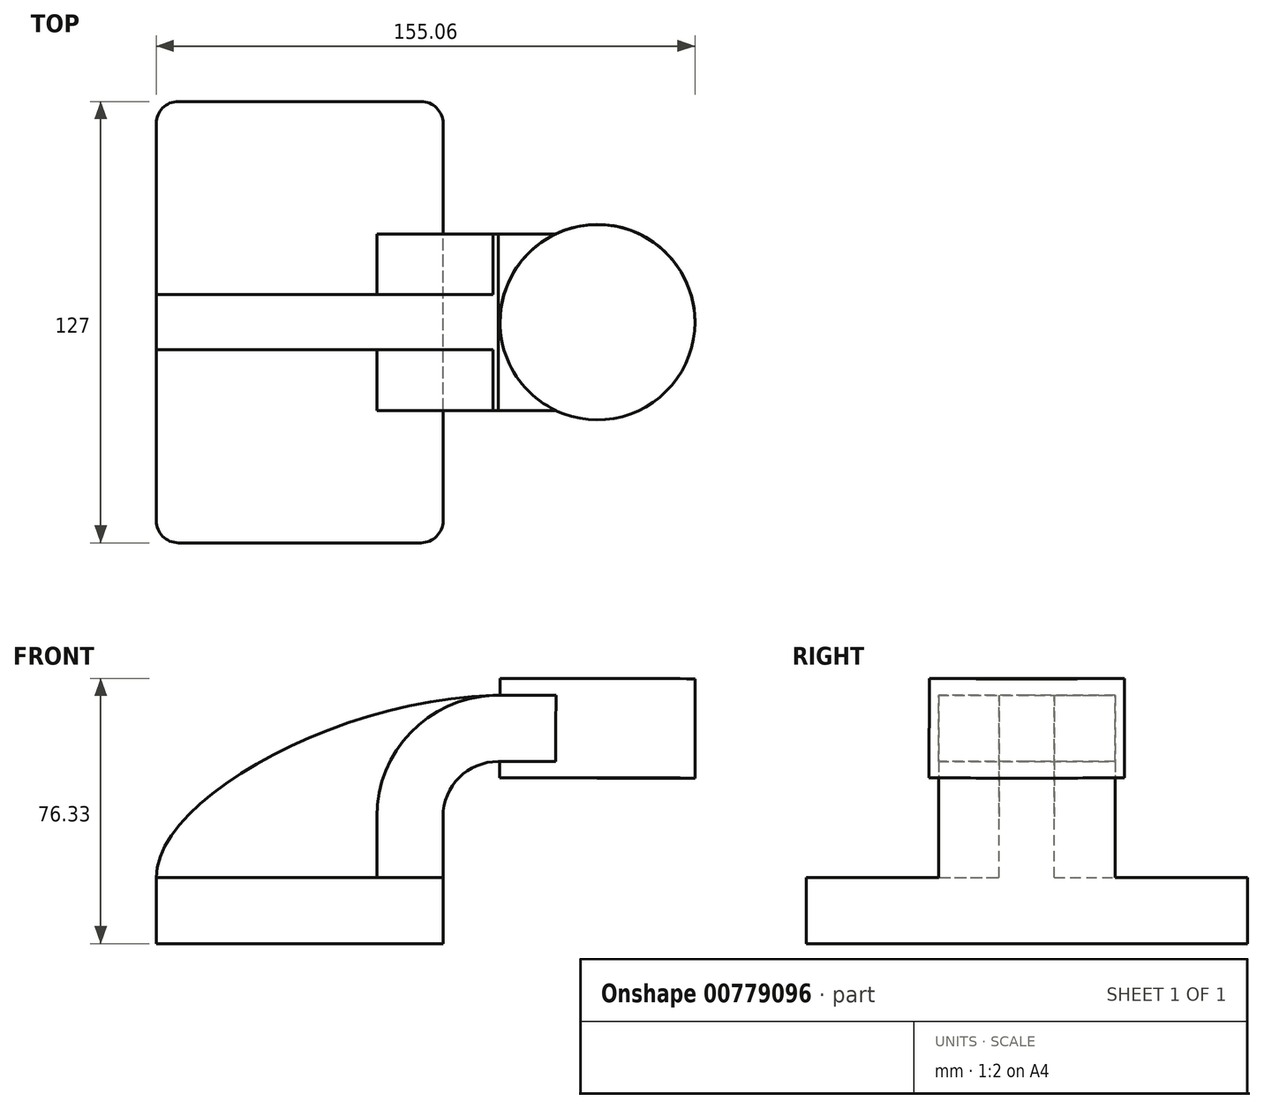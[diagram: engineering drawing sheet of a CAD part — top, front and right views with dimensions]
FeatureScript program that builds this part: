
annotation { "Feature Type Name" : "Feature", "Feature Type Description" : "" }
export const myFeature = defineFeature(function(context is Context, id is Id, definition is map)
    precondition{}
    {
        {
            var Q0;
            Q0=qCreatedBy(makeId("Front.planeOp"),FACE);
            var sketch = newSketch(context, id + "F0", { "sketchPlane" : qUnion([Q0])});
            skLineSegment(sketch, "E0.bottom", {"start": v(41.27, 9.53) * mm, "end": v(-41.28, 9.53) * mm});
            skLineSegment(sketch, "E0.top", {"start": v(41.28, -9.52) * mm, "end": v(-41.28, -9.52) * mm});
            skLineSegment(sketch, "E0.left", {"start": v(41.28, 9.53) * mm, "end": v(41.28, -9.52) * mm});
            skLineSegment(sketch, "E0.right", {"start": v(-41.28, 9.53) * mm, "end": v(-41.28, -9.52) * mm});
            skPoint(sketch, "E0.middle", {"position": v(0, 0) * mm});
            skLineSegment(sketch, "E1", {"start": v(41.27, 9.53) * mm, "end": v(41.27, 27) * mm});
            skArc(sketch, "E2", {"start": v(41.27, 27) * mm, "mid": v(45.92, 38.23) * mm, "end": v(57.15, 42.88) * mm});
            skLineSegment(sketch, "E3", {"start": v(57.15, 42.88) * mm, "end": v(85.72, 42.88) * mm});
            skLineSegment(sketch, "E4.0", {"start": v(57.15, 61.93) * mm, "end": v(85.72, 61.93) * mm});
            skArc(sketch, "E4.1", {"start": v(22.22, 27) * mm, "mid": v(32.45, 51.7) * mm, "end": v(57.15, 61.93) * mm});
            skLineSegment(sketch, "E4.2", {"start": v(22.22, 9.53) * mm, "end": v(22.22, 27) * mm});
            skLineSegment(sketch, "E5.bottom", {"start": v(113.78, 66.68) * mm, "end": v(62.98, 66.68) * mm});
            skLineSegment(sketch, "E5.top", {"start": v(113.78, 38.1) * mm, "end": v(62.98, 38.1) * mm});
            skLineSegment(sketch, "E5.left", {"start": v(113.78, 66.68) * mm, "end": v(113.78, 38.1) * mm});
            skLineSegment(sketch, "E5.right", {"start": v(62.98, 66.68) * mm, "end": v(62.98, 38.1) * mm});
            skPoint(sketch, "E5.middle", {"position": v(88.38, 52.39) * mm});
            skFitSpline(sketch, "E6", {"points": [v(-41.28, 9.53) * mm, v(57.15, 61.93) * mm], "startDerivative": vector(-0.1, 67.07) * mm, "endDerivative": vector(138.25, 2.1) * mm});
            skLineSegment(sketch, "E7", {"start": v(85.66, 38.1) * mm, "end": v(85.72, 66.68) * mm});
            skSolve(sketch);
        }
        {
            var Q0;
            Q0=makeQuery(id+"F0.imprint","IMPRINT",FACE,{"disambiguationData":[TD([[makeQuery(id+"F0.imprint","IMPRINT",EDGE,{"derivedFrom":sQuery(id+"F0.wireOp",EDGE,"E0.top")}),-1.0]])]});
            extrude(context, id + "F1", {"entities" : qUnion([Q0]), "endBound" : BoundingType.SYMMETRIC, "depth" : 127 * mm, "offsetDistance" : 25.4 * mm});
        }
        {
            var Q0;
            {var subQ4=sQuery(id+"F0.wireOp",EDGE,"E1");Q0=makeQuery(id+"F0.imprint","IMPRINT",FACE,{"disambiguationData":[TD([[makeQuery(id+"F0.imprint","IMPRINT",EDGE,{"derivedFrom":subQ4}),1.0]])]});}
            var Q1;
            {var subQ0=sQuery(id+"F0.wireOp",EDGE,"E5.right");var subQ1=sQuery(id+"F0.wireOp",EDGE,"E3");var subQ2=makeQuery(id+"F0.imprint","INTERSECT",VERTEX,{"derivedFrom":[subQ1,subQ0]});Q1=makeQuery(id+"F0.imprint","IMPRINT",FACE,{"disambiguationData":[TD([[makeQuery(id+"F0.imprint","IMPRINT",EDGE,{"disambiguationData":[TD([[subQ2,-1.0]])],"derivedFrom":subQ1}),1.0]])]});}
            extrude(context, id + "F2", {"entities" : qUnion([Q0, Q1]), "operationType" : NewBodyOperationType.ADD, "endBound" : BoundingType.SYMMETRIC, "depth" : 50.8 * mm, "offsetDistance" : 25.4 * mm});
        }
        {
            var Q0;
            {var subQ3=sQuery(id+"F0.wireOp",EDGE,"E4.2");Q0=makeQuery(id+"F0.imprint","IMPRINT",FACE,{"disambiguationData":[TD([[makeQuery(id+"F0.imprint","IMPRINT",EDGE,{"derivedFrom":subQ3}),1.0]])]});}
            extrude(context, id + "F3", {"entities" : qUnion([Q0]), "operationType" : NewBodyOperationType.ADD, "endBound" : BoundingType.SYMMETRIC, "depth" : 15.88 * mm, "offsetDistance" : 25.4 * mm});
        }
        {
            var Q0;
            {var subQ0=sQuery(id+"F0.wireOp",EDGE,"E5.left");Q0=makeQuery(id+"F0.imprint","IMPRINT",FACE,{"disambiguationData":[TD([[makeQuery(id+"F0.imprint","IMPRINT",EDGE,{"derivedFrom":subQ0}),-1.0]])]});}
            var Q1;
            Q1=sQuery(id+"F0.wireOp",EDGE,"E7");
            revolve(context, id + "F4", {"operationType" : NewBodyOperationType.ADD, "surfaceOperationType" : NewSurfaceOperationType.NEW, "entities" : qUnion([Q0]), "axis" : qUnion([Q1]), "revolveType" : RevolveType.FULL});
        }
        {
            var Q0;
            Q0=makeQuery(id+"F1.opExtrude","CAP_EDGE",EDGE,{"disambiguationData":[OSD([sQuery(id+"F0.wireOp",EDGE,"E0.right")])],"isStart":false});
            var Q1;
            Q1=makeQuery(id+"F1.opExtrude","CAP_EDGE",EDGE,{"disambiguationData":[OSD([sQuery(id+"F0.wireOp",EDGE,"E0.left")])],"isStart":false});
            var Q2;
            Q2=makeQuery(id+"F1.opExtrude","CAP_EDGE",EDGE,{"disambiguationData":[OSD([sQuery(id+"F0.wireOp",EDGE,"E0.right")])],"isStart":true});
            var Q3;
            Q3=makeQuery(id+"F1.opExtrude","CAP_EDGE",EDGE,{"disambiguationData":[OSD([sQuery(id+"F0.wireOp",EDGE,"E0.left")])],"isStart":true});
            fillet(context, id + "F5", {"entities" : qUnion([Q0, Q1, Q2, Q3]), "radius" : 6.35 * mm, "tangentPropagation" : true, "allowEdgeOverflow" : false});
        }
    });
